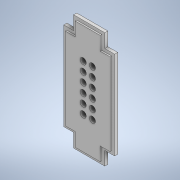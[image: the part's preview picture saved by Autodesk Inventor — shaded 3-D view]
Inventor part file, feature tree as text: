
AUTODESK INVENTOR PART (.ipt)
format: ipt  version: 2021 (Build 250183000, 183)  size: 189,440 bytes
history: native  units: mm
features: extrude x3, sketch x2
ambient origin geometry x8: Origin, YZ Plane, XZ Plane, XY Plane, X Axis, Y Axis, Z Axis, Center Point
bodies: Solid1 (feature_tree)
feature tree (5):
  sketch  "Sketch1"  dims[d0=106.84mm d1=142.4mm]
  sketch  "Sketch2"  dims[d2=17.78mm d3=17.78mm d4=32.6mm d5=12.8mm d6=12.8mm d7=4.0mm d8=4.0mm d9=4.0mm d10=4.0mm d11=4.0mm d12=4.0mm d13=4.0mm d14=4.0mm d15=4.0mm d22=8.0mm d27=8.0mm d30=8.0mm d34=8.0mm d38=8.0mm d42=8.0mm d59=12.0mm d63=12.0mm d67=12.0mm d70=12.0mm d71=12.0mm d75=12.0mm d93=12.0mm d94=0.0mm d97=0.0mm d98=12.0mm d102=0.0mm d103=12.0mm d113=6.0mm d114=0.0mm d115=4.0mm d116=0.0mm d117=12.0mm d118=0.0mm d119=0.5mm d120=0.872665mm]
  extrude  "Extrusion1"  Depth=142.4mm
  extrude  "Extrusion2"  Depth=17.78mm
  extrude  "Extrusion3"  Depth=32.6mm
